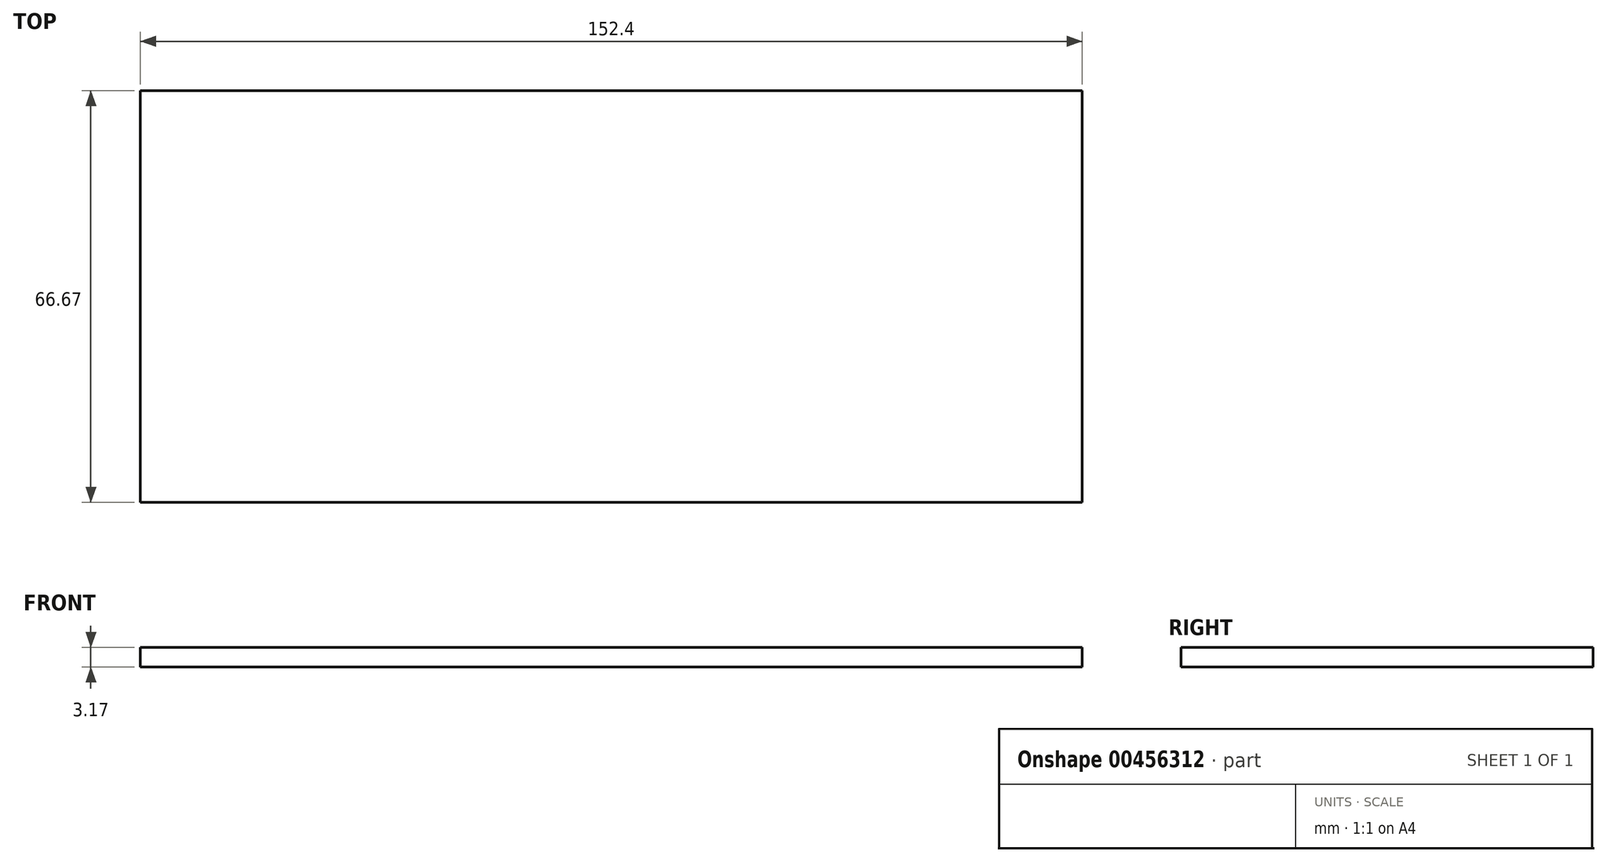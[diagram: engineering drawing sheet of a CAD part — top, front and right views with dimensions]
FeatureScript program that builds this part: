
annotation { "Feature Type Name" : "Feature", "Feature Type Description" : "" }
export const myFeature = defineFeature(function(context is Context, id is Id, definition is map)
    precondition{}
    {
        {
            var Q0;
            Q0=qCreatedBy(makeId("Top.planeOp"),FACE);
            var sketch = newSketch(context, id + "F0", { "sketchPlane" : qUnion([Q0])});
            skLineSegment(sketch, "E0.bottom", {"start": v(0, 0) * mm, "end": v(152.4, 0) * mm});
            skLineSegment(sketch, "E0.top", {"start": v(0, 66.67) * mm, "end": v(152.4, 66.67) * mm});
            skLineSegment(sketch, "E0.left", {"start": v(0, 0) * mm, "end": v(0, 66.67) * mm});
            skLineSegment(sketch, "E0.right", {"start": v(152.4, 0) * mm, "end": v(152.4, 66.68) * mm});
            skSolve(sketch);
        }
        {
            var Q0;
            Q0=makeQuery(id+"F0.imprint","IMPRINT",FACE,{"disambiguationData":[TD([[makeQuery(id+"F0.imprint","IMPRINT",EDGE,{"derivedFrom":sQuery(id+"F0.wireOp",EDGE,"E0.bottom")}),1.0]])]});
            extrude(context, id + "F1", {"entities" : qUnion([Q0]), "depth" : 3.17 * mm});
        }
    });
